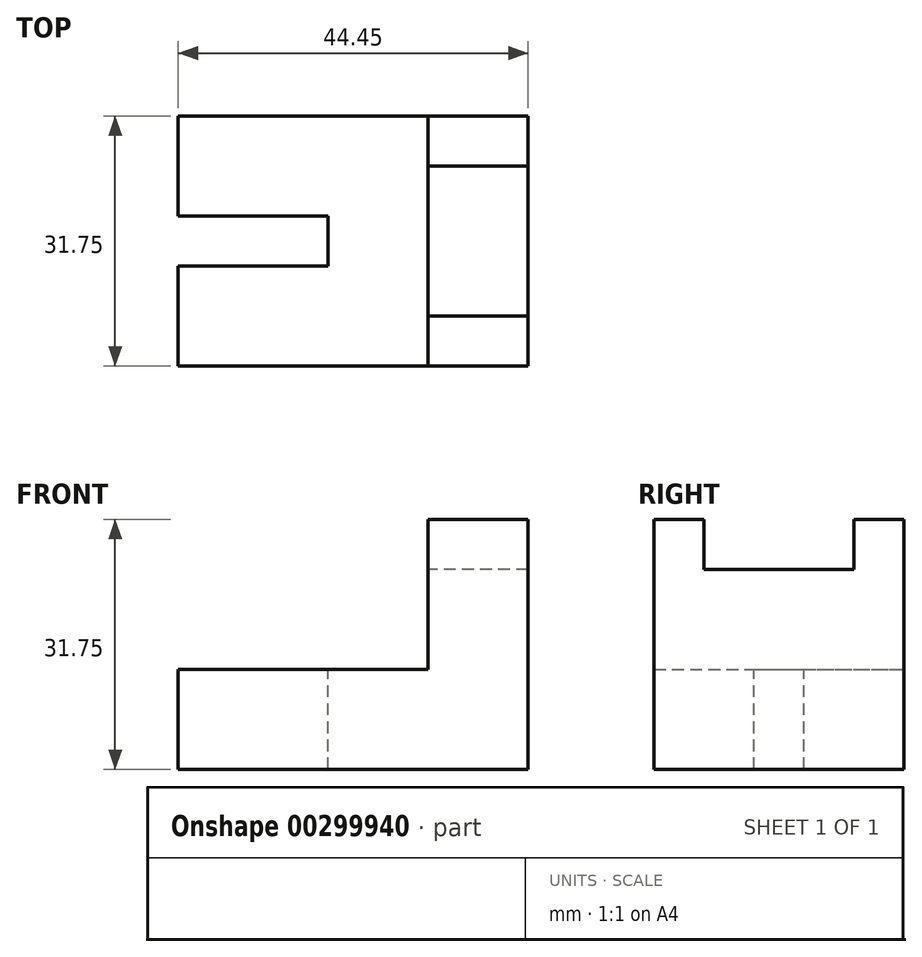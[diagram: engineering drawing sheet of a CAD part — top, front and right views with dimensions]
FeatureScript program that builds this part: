
annotation { "Feature Type Name" : "Feature", "Feature Type Description" : "" }
export const myFeature = defineFeature(function(context is Context, id is Id, definition is map)
    precondition{}
    {
        {
            var Q0;
            Q0=qCreatedBy(makeId("Front.planeOp"),FACE);
            var sketch = newSketch(context, id + "F0", { "sketchPlane" : qUnion([Q0])});
            skLineSegment(sketch, "E0.bottom", {"start": v(0, 0) * mm, "end": v(44.45, 0) * mm});
            skLineSegment(sketch, "E0.top", {"start": v(0, 12.7) * mm, "end": v(31.75, 12.7) * mm});
            skLineSegment(sketch, "E0.left", {"start": v(0, 0) * mm, "end": v(0, 12.7) * mm});
            skLineSegment(sketch, "E0.right", {"start": v(44.45, 0) * mm, "end": v(44.45, 12.7) * mm});
            skLineSegment(sketch, "E1.top", {"start": v(44.45, 31.75) * mm, "end": v(31.75, 31.75) * mm});
            skLineSegment(sketch, "E1.left", {"start": v(44.45, 12.7) * mm, "end": v(44.45, 31.75) * mm});
            skLineSegment(sketch, "E1.right", {"start": v(31.75, 12.7) * mm, "end": v(31.75, 31.75) * mm});
            skSolve(sketch);
        }
        {
            var Q0;
            Q0=makeQuery(id+"F0.imprint","IMPRINT",FACE,{"disambiguationData":[TD([[makeQuery(id+"F0.imprint","IMPRINT",EDGE,{"derivedFrom":sQuery(id+"F0.wireOp",EDGE,"E0.bottom")}),1.0]])]});
            var Q1;
            Q1=makeQuery(id+"F0.imprint","IMPRINT",FACE,{"disambiguationData":[TD([[makeQuery(id+"F0.imprint","IMPRINT",EDGE,{"derivedFrom":sQuery(id+"F0.wireOp",EDGE,"E1.bottom")}),-1.0]])]});
            extrude(context, id + "F1", {"entities" : qUnion([Q0, Q1]), "depth" : 31.75 * mm});
        }
        {
            var Q0;
            Q0=makeQuery(id+"F1.opExtrude","SWEPT_FACE",FACE,{"disambiguationData":[OSD([sQuery(id+"F0.wireOp",EDGE,"E1.right")])]});
            var sketch = newSketch(context, id + "F2", { "sketchPlane" : qUnion([Q0])});
            skLineSegment(sketch, "E2.bottom", {"start": v(6.35, 31.75) * mm, "end": v(25.4, 31.75) * mm});
            skLineSegment(sketch, "E2.top", {"start": v(6.35, 25.4) * mm, "end": v(25.4, 25.4) * mm});
            skLineSegment(sketch, "E2.left", {"start": v(6.35, 31.75) * mm, "end": v(6.35, 25.4) * mm});
            skLineSegment(sketch, "E2.right", {"start": v(25.4, 31.75) * mm, "end": v(25.4, 25.4) * mm});
            skSolve(sketch);
        }
        {
            var Q0;
            Q0=makeQuery(id+"F2.imprint","IMPRINT",FACE,{"disambiguationData":[TD([[makeQuery(id+"F2.imprint","IMPRINT",EDGE,{"derivedFrom":sQuery(id+"F2.wireOp",EDGE,"E2.bottom")}),1.0]])]});
            extrude(context, id + "F3", {"entities" : qUnion([Q0]), "operationType" : NewBodyOperationType.REMOVE, "oppositeDirection" : true, "depth" : 25.4 * mm});
        }
        {
            var Q0;
            Q0=makeQuery(id+"F1.opExtrude","SWEPT_FACE",FACE,{"disambiguationData":[OSD([sQuery(id+"F0.wireOp",EDGE,"E0.left")])]});
            var sketch = newSketch(context, id + "F4", { "sketchPlane" : qUnion([Q0])});
            skLineSegment(sketch, "E3.bottom", {"start": v(12.7, 0) * mm, "end": v(19.05, 0) * mm});
            skLineSegment(sketch, "E3.top", {"start": v(12.7, 12.7) * mm, "end": v(19.05, 12.7) * mm});
            skLineSegment(sketch, "E3.left", {"start": v(12.7, 0) * mm, "end": v(12.7, 12.7) * mm});
            skLineSegment(sketch, "E3.right", {"start": v(19.05, 0) * mm, "end": v(19.05, 12.7) * mm});
            skSolve(sketch);
        }
        {
            var Q0;
            Q0=makeQuery(id+"F4.imprint","IMPRINT",FACE,{"disambiguationData":[TD([[makeQuery(id+"F4.imprint","IMPRINT",EDGE,{"derivedFrom":sQuery(id+"F4.wireOp",EDGE,"E3.bottom")}),-1.0]])]});
            extrude(context, id + "F5", {"entities" : qUnion([Q0]), "operationType" : NewBodyOperationType.REMOVE, "oppositeDirection" : true, "depth" : 19.05 * mm});
        }
    });
